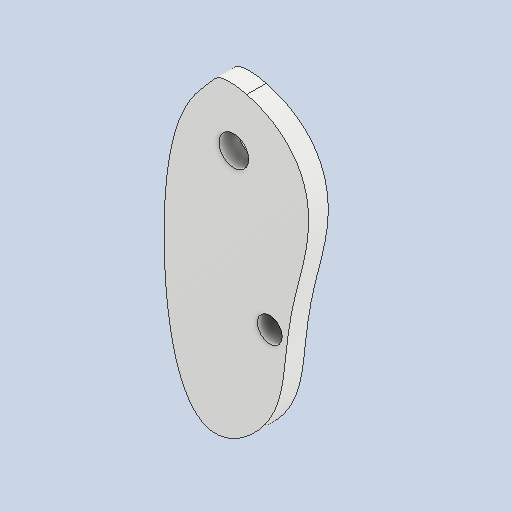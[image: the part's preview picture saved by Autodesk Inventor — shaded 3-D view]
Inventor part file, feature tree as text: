
AUTODESK INVENTOR PART (.ipt)
format: ipt  version: 2022 (Build 260153000, 153)  size: 110,080 bytes
history: native  units: in
note: dims shown in document units (in); Inventor stores cm internally (conversion verified against a paired STEP export)
features: other x3, sketch x2
ambient origin geometry x8: Origin, YZ Plane, XZ Plane, XY Plane, X Axis, Y Axis, Z Axis, Center Point
bodies: Solid1 (feature_tree)
feature tree (5):
  other  "Component35.ipt"
  other  "Solid1::Component35.ipt"
  other  "TaggingFeature1"
  sketch  "Sketch2"  dims[d0=0.3937in]
  sketch  "Sketch3"
